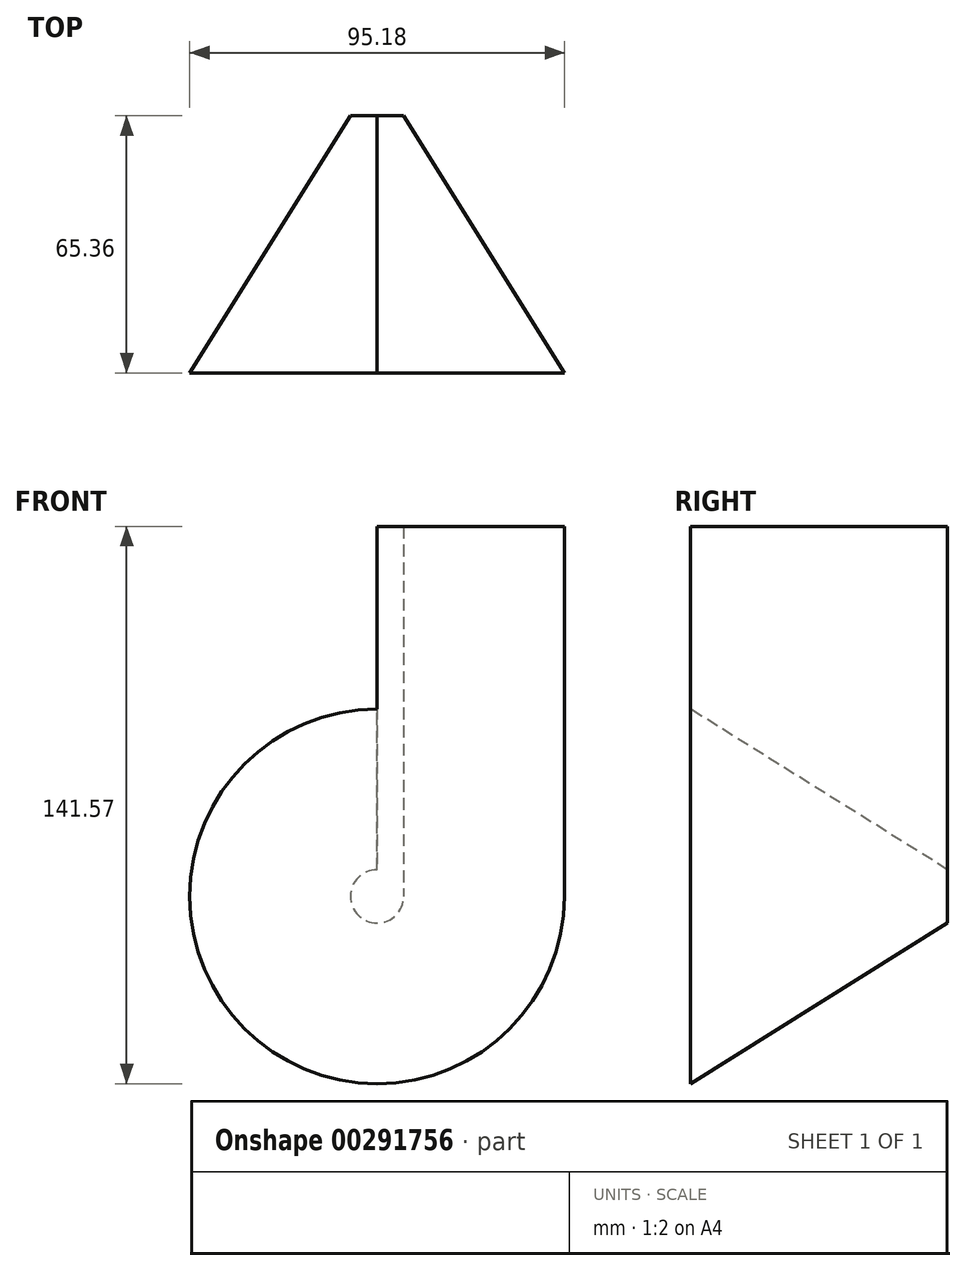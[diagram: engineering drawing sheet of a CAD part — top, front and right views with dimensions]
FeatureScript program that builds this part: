
annotation { "Feature Type Name" : "Feature", "Feature Type Description" : "" }
export const myFeature = defineFeature(function(context is Context, id is Id, definition is map)
    precondition{}
    {
        {
            var Q0;
            Q0=qCreatedBy(makeId("Top.planeOp"),FACE);
            var sketch = newSketch(context, id + "F0", { "sketchPlane" : qUnion([Q0])});
            skLineSegment(sketch, "E0", {"start": v(-36.48, 33.32) * mm, "end": v(-36.48, -32.04) * mm});
            skLineSegment(sketch, "E1", {"start": v(-36.48, -32.04) * mm, "end": v(11.11, -32.04) * mm});
            skLineSegment(sketch, "E2", {"start": v(11.11, -32.04) * mm, "end": v(-29.71, 33.32) * mm});
            skLineSegment(sketch, "E3", {"start": v(-29.71, 33.32) * mm, "end": v(-36.48, 33.32) * mm});
            skSolve(sketch);
        }
        {
            var Q0;
            Q0=makeQuery(id+"F0.imprint","IMPRINT",FACE,{"disambiguationData":[TD([[makeQuery(id+"F0.imprint","IMPRINT",EDGE,{"derivedFrom":sQuery(id+"F0.wireOp",EDGE,"E0")}),1.0]])]});
            var Q1;
            Q1=sQuery(id+"F0.wireOp",EDGE,"E0");
            revolve(context, id + "F1", {"entities" : qUnion([Q0]), "axis" : qUnion([Q1]), "revolveType" : RevolveType.FULL});
        }
        {
            var Q0;
            Q0 = qSketchRegion(id + "F0", true);
            extrude(context, id + "F2", {"entities" : qUnion([Q0]), "operationType" : NewBodyOperationType.ADD, "depth" : 93.98 * mm, "offsetDistance" : 25.4 * mm});
        }
    });
